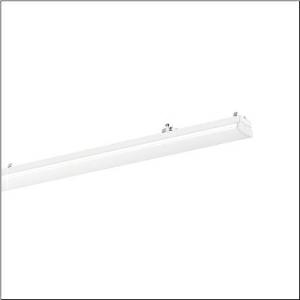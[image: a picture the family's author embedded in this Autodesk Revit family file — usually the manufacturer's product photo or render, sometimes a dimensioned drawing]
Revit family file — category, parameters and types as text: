
# Revit family: licross_11_recessed_opal_ho_51te1ddn4d5m
name_source: partatom
category: Lighting Fixtures
units: mm (PartAtom-declared; Revit-internal decimal feet)

## family parameters
Cut with Voids When Loaded = No
Host = Face
Light Source = No
Part Type = Normal
Room Calculation Point = No
Round Connector Dimension = Use Diameter
Shared = No

## types (1)
- --- (1 x LED, 13620 lm, 76.8 W, 4000K)
    Apparent Load = 77 VA
    CIE Flux Codes = 44 73 91 87 100
    Color Rendering = 80
    Color Temperature = 4000K
    Default Elevation = 1800 mm
    Description = Licross 11 recessed opal HO, luminaire insert, of sheet steel, coil coated, white, length: 1.500mm, width: 76mm, height: 87mm, LED rated luminous flux: 13.620lm, light colour: 840, SDCM (Standard Deviation of Colour Matching)MacAdam ≤ 2 SDCM (initial), control gear: DALI 2, with plug, 5-pole, with phase selection, mains connection: 220..240V, AC, 50/60Hz, rated input power: 77W, internal wiring halogen-free, primary optical cover: cover, of PMMA, light emission: direct with ceiling illumination distribution, primary light characteristic: symmetric, protection rating (complete): IP54, insulation class (complete): insulation class I (protective earthing), certification: CE, ENEC, VDE, UKCA, protection symbol: D if used in an environment with non-conductive dust loads with corresponding accessories, impact resistance: IK06, permissible ambient temperature for indoor applications: -25..+30°C, corresponds to IFS (International Featured Standards) requirements for safety and quality in the food industry, reducing of maximum allowable ambient temperature of 5°C with ceiling mounting, LABS conformity tested according to VDMA 24364:2018-05, The light source and the operating device comply with the requirements of the Ecodesign Regulation (EU) 2019/2020 and are replaceable in accordance with this regulation, packaging unit: 1 piece
    Height = 83 mm
    Lamp = 1 x LED
    Lamp Light Flux = 13620 lm
    Lamp Power = 76.8 W
    Lamp count = 1
    Length = 1500 mm
    Luminous efficacy = 177 lm/W
    Manufacturer = Siteco
    ModVariant = No
    Model = 51TE1DDN4D5M
    Mounting Place = Ceiling
    Mounting Type = Pendant
    Number of Poles = 1
    OnlyDefault = Yes
    Power Factor = 1
    Product Name = Licross 11 recessed opal HO
    Product group = luminaire insert | ceiling pendant
    ProductGroupID = 901
    Protection Class = Protection class I
    Protection Degree = IP 54
    RLX_Detail_Level = 1
    RLX_Emergency_Light_Flux = 0 lm
    RLX_Emergency_Type = 0
    RLX_Emergency_Type_DB = No
    RlxData = <blob elided: 27281 chars, md5=e8024e0e>
    Socket = socket
    Standby Power = 0 W
    System Light Flux = 13620 lm
    System Power = 77 W
    Type Comments = factory setting: luminous flux: 100 % | dim-lin: 254 | 522 mA
    Type Image = l_1313666.jpg
    URL = http://relux.com
    VarID = @adj_083605
    Voltage = 0 V
    Weight = 0.00 kg
    Width = 76 mm

## geometry (parser evidence)
native form markers: Blend x4, Sweep x14
no freeform markers — native parametric forms only
